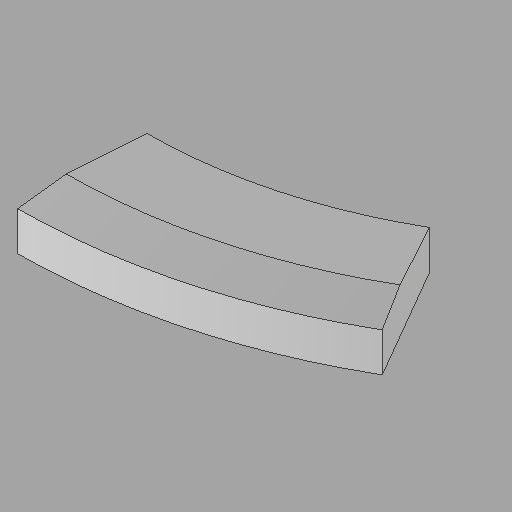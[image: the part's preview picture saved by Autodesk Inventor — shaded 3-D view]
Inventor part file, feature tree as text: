
AUTODESK INVENTOR PART (.ipt)
format: ipt  version: 2022.2 (Build 262287010, 287A)  size: 116,224 bytes
history: native  units: in
note: dims shown in document units (in); Inventor stores cm internally (conversion verified against a paired STEP export)
features: direct_edit x1, other x1, revolve x1
ambient origin geometry x8: Origin, YZ Plane, XZ Plane, XY Plane, X Axis, Y Axis, Z Axis, Center Point
bodies: Solid1 (feature_tree)
feature tree (3):
  direct_edit  "Direct Edit2"
  other  "Rad cap (2)"
  revolve  "Rotate5"  [1 undecoded]
note: 1 required parameter value undecoded (feature->parameter linkage not recoverable at this tier; creation-order binding heuristic only, values carry confidence <= 0.55)
